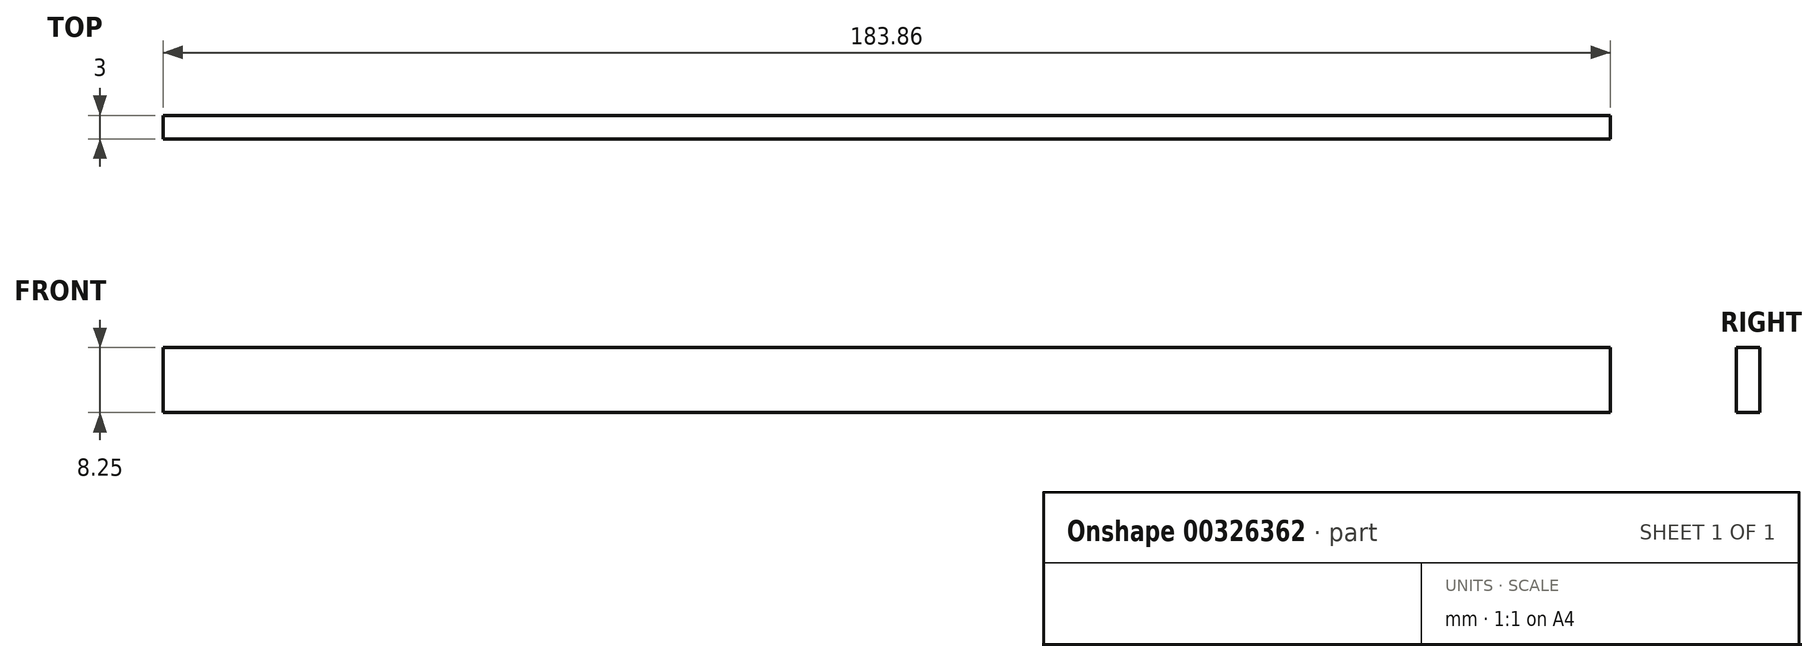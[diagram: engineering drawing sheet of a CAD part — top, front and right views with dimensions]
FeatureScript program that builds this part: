
annotation { "Feature Type Name" : "Feature", "Feature Type Description" : "" }
export const myFeature = defineFeature(function(context is Context, id is Id, definition is map)
    precondition{}
    {
        {
            var Q0;
            Q0=qCreatedBy(makeId("Front.planeOp"),FACE);
            var sketch = newSketch(context, id + "F0", { "sketchPlane" : qUnion([Q0])});
            skLineSegment(sketch, "E0.bottom", {"start": v(-91.92, 0) * mm, "end": v(91.92, 0) * mm});
            skLineSegment(sketch, "E0.top", {"start": v(-91.92, 8.25) * mm, "end": v(91.92, 8.25) * mm});
            skLineSegment(sketch, "E0.left", {"start": v(-91.92, 0) * mm, "end": v(-91.92, 8.25) * mm});
            skLineSegment(sketch, "E0.right", {"start": v(91.92, 0) * mm, "end": v(91.92, 8.25) * mm});
            skSolve(sketch);
        }
        {
            var Q0;
            Q0=makeQuery(id+"F0.imprint","IMPRINT",FACE,{"disambiguationData":[TD([[makeQuery(id+"F0.imprint","IMPRINT",EDGE,{"derivedFrom":sQuery(id+"F0.wireOp",EDGE,"E0.bottom")}),1.0]])]});
            extrude(context, id + "F1", {"entities" : qUnion([Q0]), "depth" : 3 * mm});
        }
    });
